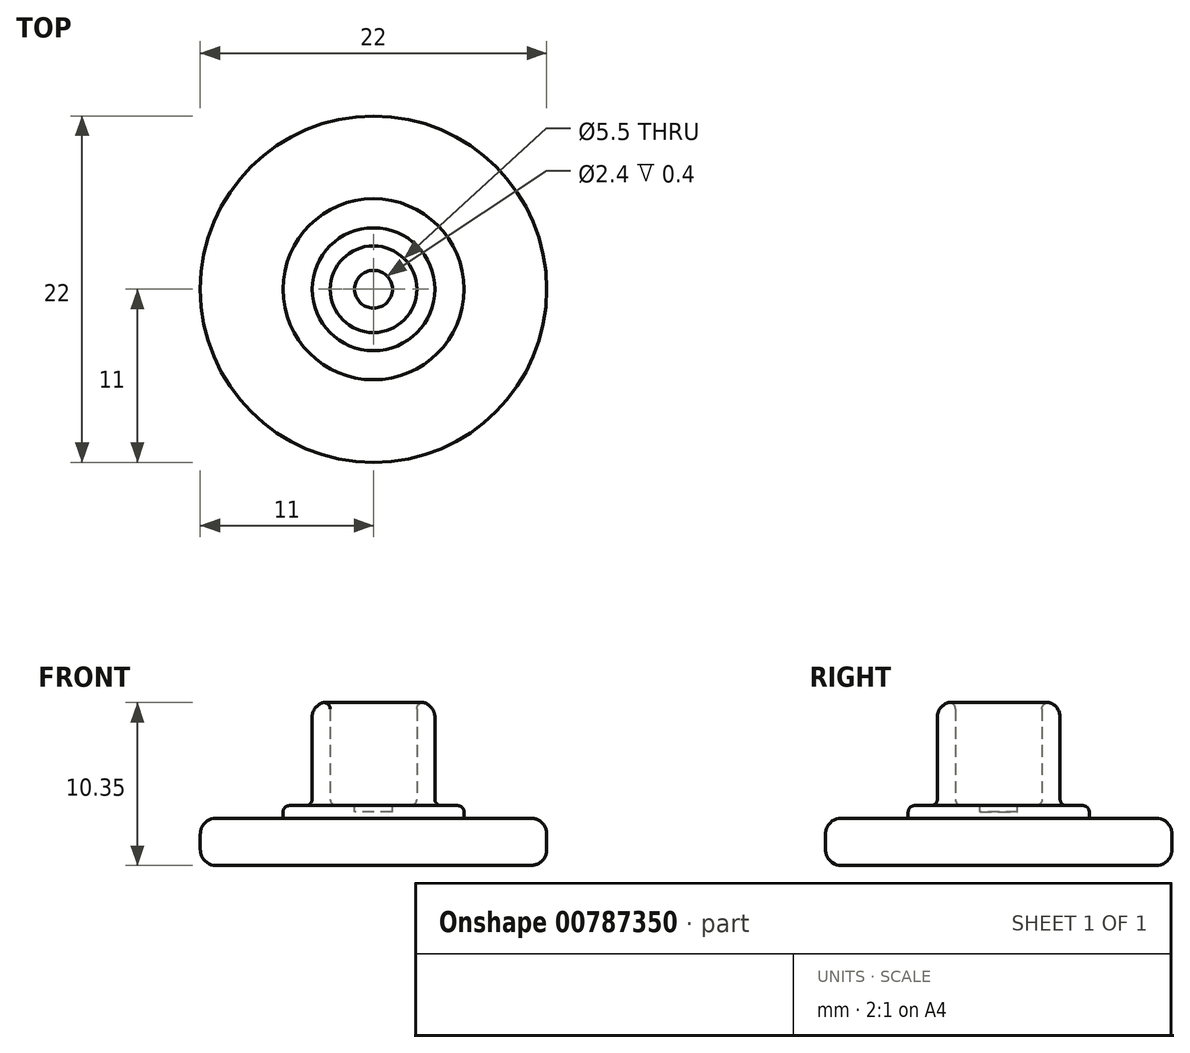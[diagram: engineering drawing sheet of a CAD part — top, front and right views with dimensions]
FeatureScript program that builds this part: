
annotation { "Feature Type Name" : "Feature", "Feature Type Description" : "" }
export const myFeature = defineFeature(function(context is Context, id is Id, definition is map)
    precondition{}
    {
        {
            var Q0;
            Q0=qCreatedBy(makeId("Top.planeOp"),FACE);
            var sketch = newSketch(context, id + "F0", { "sketchPlane" : qUnion([Q0])});
            skCircle(sketch, "E0", {"center": v(0, 0) * mm, "radius": 11 * mm});
            skSolve(sketch);
        }
        {
            var Q0;
            Q0=qSketchRegion(id+"F0",true);
            extrude(context, id + "F1", {"entities" : qUnion([Q0]), "depth" : 3 * mm});
        }
        {
            var Q0;
            Q0=makeQuery(id+"F1.opExtrude","CAP_FACE",FACE,{"disambiguationData":[OSD([sQuery(id+"F0.wireOp",EDGE,"E0")])],"isStart":false});
            var sketch = newSketch(context, id + "F2", { "sketchPlane" : qUnion([Q0])});
            skCircle(sketch, "E1", {"center": v(0, 0) * mm, "radius": 5.75 * mm});
            skSolve(sketch);
        }
        {
            var Q0;
            Q0=qSketchRegion(id+"F2",true);
            extrude(context, id + "F3", {"entities" : qUnion([Q0]), "operationType" : NewBodyOperationType.ADD, "depth" : .8 * mm, "offsetDistance" : 25 * mm});
        }
        {
            var Q0;
            Q0=makeQuery(id+"F3.opExtrude","CAP_FACE",FACE,{"disambiguationData":[OSD([sQuery(id+"F2.wireOp",EDGE,"E1")])],"isStart":false});
            var sketch = newSketch(context, id + "F4", { "sketchPlane" : qUnion([Q0])});
            skCircle(sketch, "E2", {"center": v(0, 0) * mm, "radius": 2.75 * mm});
            skCircle(sketch, "E3", {"center": v(0, 0) * mm, "radius": 3.9 * mm});
            skSolve(sketch);
        }
        {
            var Q0;
            Q0=qSketchRegion(id+"F4",true);
            extrude(context, id + "F5", {"entities" : qUnion([Q0]), "operationType" : NewBodyOperationType.ADD, "offsetDistance" : 25 * mm, "depth" : 6.6 * mm});
        }
        {
            var Q0;
            Q0=makeQuery(id+"F5.opExtrude","CAP_FACE",FACE,{"disambiguationData":[OSD([sQuery(id+"F4.wireOp",EDGE,"E2")])],"isStart":false});
            var sketch = newSketch(context, id + "F6", { "sketchPlane" : qUnion([Q0])});
            skCircle(sketch, "E4", {"center": v(0, 0) * mm, "radius": 1.2 * mm});
            skSolve(sketch);
        }
        {
            var Q0;
            {var subQ0=sQuery(id+"F2.wireOp",EDGE,"E1");Q0=makeQuery(id+"F5.boolean.opBoolean","SPLIT",FACE,{"disambiguationData":[TD([makeQuery(id+"F3.opExtrude","SWEPT_FACE",FACE,{"disambiguationData":[OSD([subQ0])]})])],"derivedFrom":makeQuery(id+"F3.opExtrude","CAP_FACE",FACE,{"disambiguationData":[OSD([subQ0])],"isStart":false})});}
            cPlane(context, id + "F7", {"entities" : qUnion([Q0]), "cplaneType" : CPlaneType.OFFSET, "offset" : 1 * mm, "width" : 152.4 * mm, "height" : 152.4 * mm});
        }
        {
            var Q0;
            Q0=qCreatedBy(id+"F7.planeOp",FACE);
            var sketch = newSketch(context, id + "F8", { "sketchPlane" : qUnion([Q0])});
            skCircle(sketch, "E5", {"center": v(0, 0) * mm, "radius": 2 * mm});
            skCircle(sketch, "E6", {"center": v(0, 0) * mm, "radius": 2.4 * mm});
            skSolve(sketch);
        }
        {
            var Q0;
            Q0=makeQuery(id+"F8.imprint","IMPRINT",FACE,{"disambiguationData":[TD([[makeQuery(id+"F8.imprint","IMPRINT",EDGE,{"derivedFrom":sQuery(id+"F8.wireOp",EDGE,"E5")}),-1.0]])]});
            extrude(context, id + "F9", {"entities" : qUnion([Q0]), "operationType" : NewBodyOperationType.REMOVE, "depth" : 0.6 * mm});
        }
        {
            var Q0;
            Q0=qSketchRegion(id+"F6",true);
            extrude(context, id + "F10", {"entities" : qUnion([Q0]), "operationType" : NewBodyOperationType.REMOVE, "oppositeDirection" : true, "depth" : 7 * mm});
        }
        {
            var Q0;
            Q0=makeQuery(id+"F1.opExtrude","CAP_EDGE",EDGE,{"disambiguationData":[OSD([sQuery(id+"F0.wireOp",EDGE,"E0")])],"isStart":false});
            var Q1;
            Q1=makeQuery(id+"F1.opExtrude","CAP_EDGE",EDGE,{"disambiguationData":[OSD([sQuery(id+"F0.wireOp",EDGE,"E0")])],"isStart":true});
            var Q2;
            Q2=makeQuery(id+"F5.opExtrude","CAP_EDGE",EDGE,{"disambiguationData":[OSD([sQuery(id+"F4.wireOp",EDGE,"E3")])],"isStart":false});
            fillet(context, id + "F11", {"entities" : qUnion([Q0, Q1, Q2]), "radius" : 1 * mm, "tangentPropagation" : true, "allowEdgeOverflow" : false});
        }
        {
            var Q0;
            {var subQ0=sQuery(id+"F2.wireOp",EDGE,"E1");Q0=makeQuery(id+"F5.boolean.opBoolean","SPLIT",FACE,{"disambiguationData":[TD([makeQuery(id+"F3.opExtrude","SWEPT_FACE",FACE,{"disambiguationData":[OSD([subQ0])]})])],"derivedFrom":makeQuery(id+"F3.opExtrude","CAP_FACE",FACE,{"disambiguationData":[OSD([subQ0])],"isStart":false})});}
            var Q1;
            Q1=makeQuery(id+"F5.opExtrude","CAP_FACE",FACE,{"disambiguationData":[OSD([sQuery(id+"F4.wireOp",EDGE,"E2"),sQuery(id+"F4.wireOp",EDGE,"E3")])],"isStart":false});
            var Q2;
            Q2=makeQuery(id+"F5.opExtrude","CAP_EDGE",EDGE,{"disambiguationData":[OSD([sQuery(id+"F4.wireOp",EDGE,"E2")])],"isStart":true});
            var Q3;
            Q3=makeQuery(id+"F3.opExtrude","CAP_EDGE",EDGE,{"disambiguationData":[OSD([sQuery(id+"F2.wireOp",EDGE,"E1")])],"isStart":true});
            fillet(context, id + "F12", {"entities" : qUnion([Q0, Q1, Q2, Q3]), "radius" : .4 * mm, "tangentPropagation" : true, "allowEdgeOverflow" : false});
        }
    });
